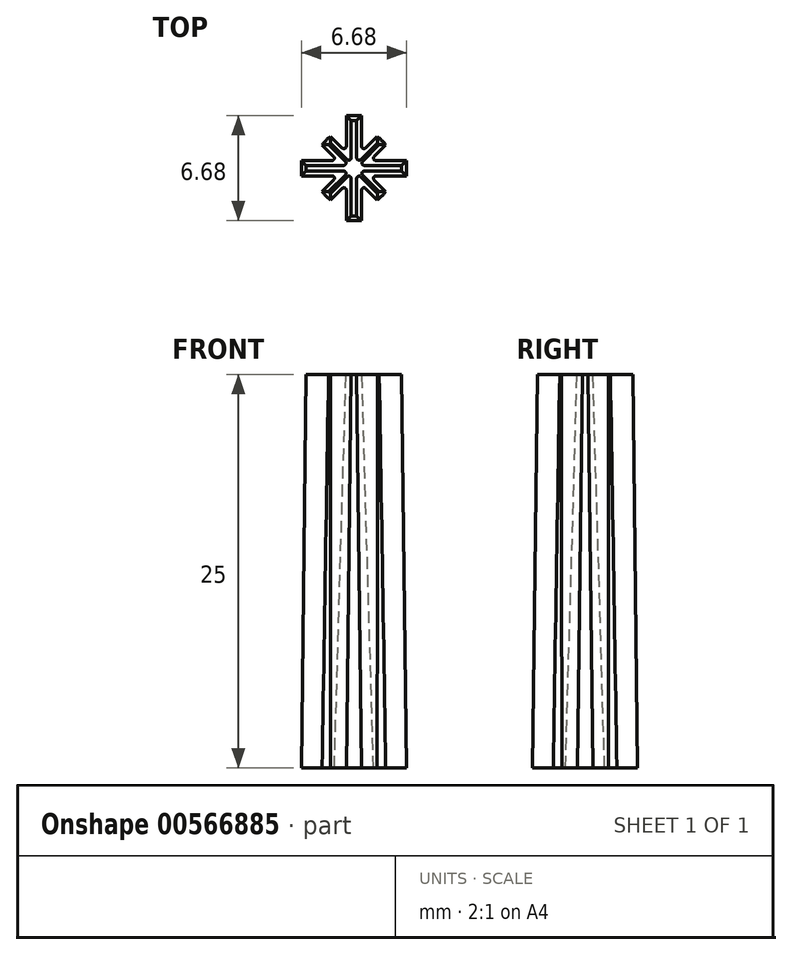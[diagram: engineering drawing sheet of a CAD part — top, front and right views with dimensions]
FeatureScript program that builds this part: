
annotation { "Feature Type Name" : "Feature", "Feature Type Description" : "" }
export const myFeature = defineFeature(function(context is Context, id is Id, definition is map)
    precondition{}
    {
        {
            var Q0;
            Q0=qCreatedBy(makeId("Top.planeOp"),FACE);
            var sketch = newSketch(context, id + "F0", { "sketchPlane" : qUnion([Q0])});
            skPoint(sketch, "E0.orphan", {"position": v(3.7, -3.7) * mm});
            skPoint(sketch, "E1.orphan", {"position": v(-3.7, -3.7) * mm});
            skPoint(sketch, "E2.orphan", {"position": v(-3.7, 3.7) * mm});
            skLineSegment(sketch, "E3", {"start": v(0.25, 0.49) * mm, "end": v(0.25, 3.06) * mm});
            skPoint(sketch, "E4.end.orphan", {"position": v(0, 2.16) * mm});
            skLineSegment(sketch, "E5.trimOffspring", {"start": v(0, 2.16) * mm, "end": v(0, -4.41) * mm, "construction": true});
            skLineSegment(sketch, "E6", {"start": v(0.25, 3.34) * mm, "end": v(0, 3.34) * mm});
            skLineSegment(sketch, "E7", {"start": v(0, 3.06) * mm, "end": v(0.25, 3.06) * mm});
            skLineSegment(sketch, "E8", {"start": v(0.25, 3.34) * mm, "end": v(0.49, 3.34) * mm});
            skLineSegment(sketch, "E9", {"start": v(0.49, 3.34) * mm, "end": v(0.49, 2.45) * mm});
            skArc(sketch, "E10", {"start": v(1.63, 1.63) * mm, "mid": v(1.57, 1.69) * mm, "end": v(1.5, 1.74) * mm});
            skLineSegment(sketch, "E11", {"start": v(0.49, 2.45) * mm, "end": v(0.49, 1.03) * mm});
            skLineSegment(sketch, "E12", {"start": v(0, 0) * mm, "end": v(3.45, 3.45) * mm, "construction": true});
            skPoint(sketch, "E13.orphan", {"position": v(0.25, 0) * mm});
            skLineSegment(sketch, "E14", {"start": v(0.49, 1.03) * mm, "end": v(1.34, 1.88) * mm});
            skLineSegment(sketch, "E15", {"start": v(1.5, 1.74) * mm, "end": v(0.25, 0.49) * mm});
            skLineSegment(sketch, "E16", {"start": v(1.34, 1.88) * mm, "end": v(1.47, 2.02) * mm});
            skLineSegment(sketch, "E17", {"start": v(1.63, 1.63) * mm, "end": v(1.77, 1.77) * mm});
            skArc(sketch, "E18.trimOffspring", {"start": v(1.77, 1.77) * mm, "mid": v(1.63, 1.9) * mm, "end": v(1.47, 2.02) * mm});
            skArc(sketch, "E19.MirrorCS", {"start": v(1.77, 1.77) * mm, "mid": v(1.9, 1.63) * mm, "end": v(2.02, 1.47) * mm});
            skArc(sketch, "E20.MirrorCS", {"start": v(1.63, 1.63) * mm, "mid": v(1.69, 1.57) * mm, "end": v(1.74, 1.5) * mm});
            skLineSegment(sketch, "E21.MirrorCS", {"start": v(1.88, 1.34) * mm, "end": v(2.02, 1.47) * mm});
            skLineSegment(sketch, "E22.MirrorCS", {"start": v(1.03, 0.49) * mm, "end": v(1.88, 1.34) * mm});
            skLineSegment(sketch, "E23.MirrorCS", {"start": v(1.74, 1.5) * mm, "end": v(0.49, 0.25) * mm});
            skLineSegment(sketch, "E24.MirrorCS", {"start": v(2.45, 0.49) * mm, "end": v(1.03, 0.49) * mm});
            skLineSegment(sketch, "E25.MirrorCS", {"start": v(3.06, 0) * mm, "end": v(3.06, 0.25) * mm});
            skLineSegment(sketch, "E26.MirrorCS", {"start": v(3.34, 0.25) * mm, "end": v(3.34, 0.49) * mm});
            skLineSegment(sketch, "E27.MirrorCS", {"start": v(3.34, 0.25) * mm, "end": v(3.34, 0) * mm});
            skLineSegment(sketch, "E28.MirrorCS", {"start": v(6.6, 0) * mm, "end": v(2.5, 0) * mm, "construction": true});
            skLineSegment(sketch, "E29.MirrorCS", {"start": v(6.6, 0) * mm, "end": v(3.34, 0) * mm, "construction": true});
            skLineSegment(sketch, "E30.MirrorCS", {"start": v(3.34, 0.49) * mm, "end": v(2.45, 0.49) * mm});
            skPoint(sketch, "E31.orphan", {"position": v(0, 6.6) * mm});
            skPoint(sketch, "E32.orphan", {"position": v(0, 2.5) * mm});
            skLineSegment(sketch, "E33.trimOffspring", {"start": v(3.06, 0) * mm, "end": v(2.5, 0) * mm, "construction": true});
            skLineSegment(sketch, "E34.MirrorCS", {"start": v(0, 3.06) * mm, "end": v(-0.25, 3.06) * mm});
            skLineSegment(sketch, "E35.MirrorCS", {"start": v(-0.25, 3.34) * mm, "end": v(0, 3.34) * mm});
            skLineSegment(sketch, "E36.MirrorCS", {"start": v(-0.25, 3.34) * mm, "end": v(-0.49, 3.34) * mm});
            skLineSegment(sketch, "E37.MirrorCS", {"start": v(-0.49, 3.34) * mm, "end": v(-0.49, 2.45) * mm});
            skLineSegment(sketch, "E38.MirrorCS", {"start": v(-0.49, 1.03) * mm, "end": v(-1.34, 1.88) * mm});
            skLineSegment(sketch, "E39.MirrorCS", {"start": v(-1.34, 1.88) * mm, "end": v(-1.47, 2.02) * mm});
            skArc(sketch, "E40.MirrorCS", {"start": v(-1.77, 1.77) * mm, "mid": v(-1.63, 1.9) * mm, "end": v(-1.47, 2.02) * mm});
            skArc(sketch, "E41.MirrorCS", {"start": v(-1.77, 1.77) * mm, "mid": v(-1.9, 1.63) * mm, "end": v(-2.02, 1.47) * mm});
            skLineSegment(sketch, "E42.MirrorCS", {"start": v(-1.88, 1.34) * mm, "end": v(-2.02, 1.47) * mm});
            skArc(sketch, "E43.MirrorCS", {"start": v(-1.63, 1.63) * mm, "mid": v(-1.69, 1.57) * mm, "end": v(-1.74, 1.5) * mm});
            skArc(sketch, "E44.MirrorCS", {"start": v(-1.63, 1.63) * mm, "mid": v(-1.57, 1.69) * mm, "end": v(-1.5, 1.74) * mm});
            skLineSegment(sketch, "E45.MirrorCS", {"start": v(-0.49, 2.45) * mm, "end": v(-0.49, 1.03) * mm});
            skLineSegment(sketch, "E46.MirrorCS", {"start": v(-3.06, 0) * mm, "end": v(-3.06, 0.25) * mm});
            skLineSegment(sketch, "E47.MirrorCS", {"start": v(-3.34, 0.25) * mm, "end": v(-3.34, 0) * mm});
            skLineSegment(sketch, "E48.MirrorCS", {"start": v(-3.34, 0.25) * mm, "end": v(-3.34, 0.49) * mm});
            skLineSegment(sketch, "E49.MirrorCS", {"start": v(-3.34, 0.49) * mm, "end": v(-2.45, 0.49) * mm});
            skLineSegment(sketch, "E50.MirrorCS", {"start": v(-2.45, 0.49) * mm, "end": v(-1.03, 0.49) * mm});
            skLineSegment(sketch, "E51.MirrorCS", {"start": v(-1.03, 0.49) * mm, "end": v(-1.88, 1.34) * mm});
            skLineSegment(sketch, "E52.MirrorCS", {"start": v(-3.34, -0.25) * mm, "end": v(-3.34, 0) * mm});
            skLineSegment(sketch, "E53.MirrorCS", {"start": v(-3.34, -0.25) * mm, "end": v(-3.34, -0.49) * mm});
            skLineSegment(sketch, "E54.MirrorCS", {"start": v(-3.06, 0) * mm, "end": v(-3.06, -0.25) * mm});
            skLineSegment(sketch, "E55.MirrorCS", {"start": v(-3.34, -0.49) * mm, "end": v(-2.45, -0.49) * mm});
            skLineSegment(sketch, "E56.MirrorCS", {"start": v(-2.45, -0.49) * mm, "end": v(-1.03, -0.49) * mm});
            skLineSegment(sketch, "E57.MirrorCS", {"start": v(-1.03, -0.49) * mm, "end": v(-1.88, -1.34) * mm});
            skLineSegment(sketch, "E58.MirrorCS", {"start": v(-1.88, -1.34) * mm, "end": v(-2.02, -1.47) * mm});
            skArc(sketch, "E59.MirrorCS", {"start": v(-1.77, -1.77) * mm, "mid": v(-1.9, -1.63) * mm, "end": v(-2.02, -1.47) * mm});
            skArc(sketch, "E60.MirrorCS", {"start": v(-1.77, -1.77) * mm, "mid": v(-1.63, -1.9) * mm, "end": v(-1.47, -2.02) * mm});
            skLineSegment(sketch, "E61.MirrorCS", {"start": v(-1.34, -1.88) * mm, "end": v(-1.47, -2.02) * mm});
            skLineSegment(sketch, "E62.MirrorCS", {"start": v(-0.49, -1.03) * mm, "end": v(-1.34, -1.88) * mm});
            skLineSegment(sketch, "E63.MirrorCS", {"start": v(-0.49, -2.45) * mm, "end": v(-0.49, -1.03) * mm});
            skLineSegment(sketch, "E64.MirrorCS", {"start": v(-0.49, -3.34) * mm, "end": v(-0.49, -2.45) * mm});
            skLineSegment(sketch, "E65.MirrorCS", {"start": v(-0.25, -3.34) * mm, "end": v(-0.49, -3.34) * mm});
            skLineSegment(sketch, "E66.MirrorCS", {"start": v(-0.25, -3.34) * mm, "end": v(0, -3.34) * mm});
            skLineSegment(sketch, "E67.MirrorCS", {"start": v(0.25, -3.34) * mm, "end": v(0, -3.34) * mm});
            skLineSegment(sketch, "E68.MirrorCS", {"start": v(0.25, -3.34) * mm, "end": v(0.49, -3.34) * mm});
            skLineSegment(sketch, "E69.MirrorCS", {"start": v(0, -3.06) * mm, "end": v(0.25, -3.06) * mm});
            skLineSegment(sketch, "E70.MirrorCS", {"start": v(0, -3.06) * mm, "end": v(-0.25, -3.06) * mm});
            skLineSegment(sketch, "E71.MirrorCS", {"start": v(0.49, -3.34) * mm, "end": v(0.49, -2.45) * mm});
            skLineSegment(sketch, "E72.MirrorCS", {"start": v(0.49, -2.45) * mm, "end": v(0.49, -1.03) * mm});
            skLineSegment(sketch, "E73.MirrorCS", {"start": v(0.49, -1.03) * mm, "end": v(1.34, -1.88) * mm});
            skLineSegment(sketch, "E74.MirrorCS", {"start": v(1.34, -1.88) * mm, "end": v(1.47, -2.02) * mm});
            skArc(sketch, "E75.MirrorCS", {"start": v(1.77, -1.77) * mm, "mid": v(1.63, -1.9) * mm, "end": v(1.47, -2.02) * mm});
            skArc(sketch, "E76.MirrorCS", {"start": v(1.77, -1.77) * mm, "mid": v(1.9, -1.63) * mm, "end": v(2.02, -1.47) * mm});
            skArc(sketch, "E77.MirrorCS", {"start": v(1.63, -1.63) * mm, "mid": v(1.57, -1.69) * mm, "end": v(1.5, -1.74) * mm});
            skArc(sketch, "E78.MirrorCS", {"start": v(1.63, -1.63) * mm, "mid": v(1.69, -1.57) * mm, "end": v(1.74, -1.5) * mm});
            skLineSegment(sketch, "E79.MirrorCS", {"start": v(1.88, -1.34) * mm, "end": v(2.02, -1.47) * mm});
            skLineSegment(sketch, "E80.MirrorCS", {"start": v(1.03, -0.49) * mm, "end": v(1.88, -1.34) * mm});
            skLineSegment(sketch, "E81.MirrorCS", {"start": v(2.45, -0.49) * mm, "end": v(1.03, -0.49) * mm});
            skLineSegment(sketch, "E82.MirrorCS", {"start": v(3.34, -0.49) * mm, "end": v(2.45, -0.49) * mm});
            skLineSegment(sketch, "E83.MirrorCS", {"start": v(3.34, -0.25) * mm, "end": v(3.34, -0.49) * mm});
            skLineSegment(sketch, "E84.MirrorCS", {"start": v(3.34, -0.25) * mm, "end": v(3.34, 0) * mm});
            skPoint(sketch, "E85.MirrorCS.end.orphan", {"position": v(-0.25, -0.49) * mm});
            skPoint(sketch, "E85.MirrorCS.start.orphan", {"position": v(-1.5, -1.74) * mm});
            skPoint(sketch, "E86.MirrorCS.end.orphan", {"position": v(-0.49, -0.25) * mm});
            skPoint(sketch, "E86.MirrorCS.start.orphan", {"position": v(-1.74, -1.5) * mm});
            skPoint(sketch, "E87.MirrorCS.start.orphan", {"position": v(-1.63, -1.63) * mm});
            skPoint(sketch, "E88.MirrorCS.end.orphan", {"position": v(-3.06, -0.25) * mm});
            skPoint(sketch, "E89.MirrorCS.end.orphan", {"position": v(-3.06, 0.25) * mm});
            skPoint(sketch, "E89.MirrorCS.start.orphan", {"position": v(-0.49, 0.25) * mm});
            skPoint(sketch, "E90.MirrorCS.start.orphan", {"position": v(-1.74, 1.5) * mm});
            skPoint(sketch, "E91.MirrorCS.end.orphan", {"position": v(-0.25, 0.49) * mm});
            skPoint(sketch, "E91.MirrorCS.start.orphan", {"position": v(-1.5, 1.74) * mm});
            skPoint(sketch, "E92.MirrorCS.end.orphan", {"position": v(-0.25, 3.06) * mm});
            skPoint(sketch, "E93.MirrorCS.end.orphan", {"position": v(3.06, 0.25) * mm});
            skPoint(sketch, "E93.MirrorCS.start.orphan", {"position": v(0.49, 0.25) * mm});
            skPoint(sketch, "E94.MirrorCS.end.orphan", {"position": v(3.06, -0.25) * mm});
            skPoint(sketch, "E94.MirrorCS.start.orphan", {"position": v(0.49, -0.25) * mm});
            skPoint(sketch, "E95.MirrorCS.start.orphan", {"position": v(1.74, -1.5) * mm});
            skPoint(sketch, "E96.MirrorCS.end.orphan", {"position": v(0.25, -3.06) * mm});
            skPoint(sketch, "E96.MirrorCS.start.orphan", {"position": v(0.25, -0.49) * mm});
            skPoint(sketch, "E97.MirrorCS.start.orphan", {"position": v(1.5, -1.74) * mm});
            skPoint(sketch, "E98.MirrorCS.end.orphan", {"position": v(-0.25, -3.06) * mm});
            skPoint(sketch, "E99.MirrorCS.start.orphan", {"position": v(3.06, 0) * mm});
            skSolve(sketch);
        }
        {
            var Q0;
            Q0 = qSketchRegion(id + "F0", true);
            extrude(context, id + "F1", {"entities" : qUnion([Q0]), "depth" : 25 * mm, "offsetDistance" : 25 * mm, "hasDraft" : true, "draftAngle" : .7 * degree, "draftPullDirection" : true});
        }
        {
            var Q0;
            Q0=makeQuery(id+"F1.opExtrude","SWEPT_EDGE",EDGE,{"disambiguationData":[OSD([sQuery(id+"F0.wireOp",EDGE,"E50.MirrorCS"),sQuery(id+"F0.wireOp",EDGE,"E51.MirrorCS")])]});
            var Q1;
            Q1=makeQuery(id+"F1.opExtrude","SWEPT_EDGE",EDGE,{"disambiguationData":[OSD([sQuery(id+"F0.wireOp",EDGE,"E56.MirrorCS"),sQuery(id+"F0.wireOp",EDGE,"E57.MirrorCS")])]});
            var Q2;
            Q2=makeQuery(id+"F1.opExtrude","SWEPT_EDGE",EDGE,{"disambiguationData":[OSD([sQuery(id+"F0.wireOp",EDGE,"E62.MirrorCS"),sQuery(id+"F0.wireOp",EDGE,"E63.MirrorCS")])]});
            var Q3;
            Q3=makeQuery(id+"F1.opExtrude","SWEPT_EDGE",EDGE,{"disambiguationData":[OSD([sQuery(id+"F0.wireOp",EDGE,"E72.MirrorCS"),sQuery(id+"F0.wireOp",EDGE,"E73.MirrorCS")])]});
            var Q4;
            Q4=makeQuery(id+"F1.opExtrude","SWEPT_EDGE",EDGE,{"disambiguationData":[OSD([sQuery(id+"F0.wireOp",EDGE,"E80.MirrorCS"),sQuery(id+"F0.wireOp",EDGE,"E81.MirrorCS")])]});
            var Q5;
            Q5=makeQuery(id+"F1.opExtrude","SWEPT_EDGE",EDGE,{"disambiguationData":[OSD([sQuery(id+"F0.wireOp",EDGE,"E22.MirrorCS"),sQuery(id+"F0.wireOp",EDGE,"E24.MirrorCS")])]});
            var Q6;
            Q6=makeQuery(id+"F1.opExtrude","SWEPT_EDGE",EDGE,{"disambiguationData":[OSD([sQuery(id+"F0.wireOp",EDGE,"E11"),sQuery(id+"F0.wireOp",EDGE,"E14")])]});
            var Q7;
            Q7=makeQuery(id+"F1.opExtrude","SWEPT_EDGE",EDGE,{"disambiguationData":[OSD([sQuery(id+"F0.wireOp",EDGE,"E38.MirrorCS"),sQuery(id+"F0.wireOp",EDGE,"E45.MirrorCS")])]});
            var Q8;
            Q8=makeQuery(id+"F1.opExtrude","CAP_EDGE",EDGE,{"disambiguationData":[OSD([sQuery(id+"F0.wireOp",EDGE,"E89.MirrorCS")])],"isStart":false});
            fillet(context, id + "F2", {"entities" : qUnion([Q0, Q1, Q2, Q3, Q4, Q5, Q6, Q7, Q8]), "radius" : .15 * mm, "tangentPropagation" : true, "allowEdgeOverflow" : false});
        }
    });
